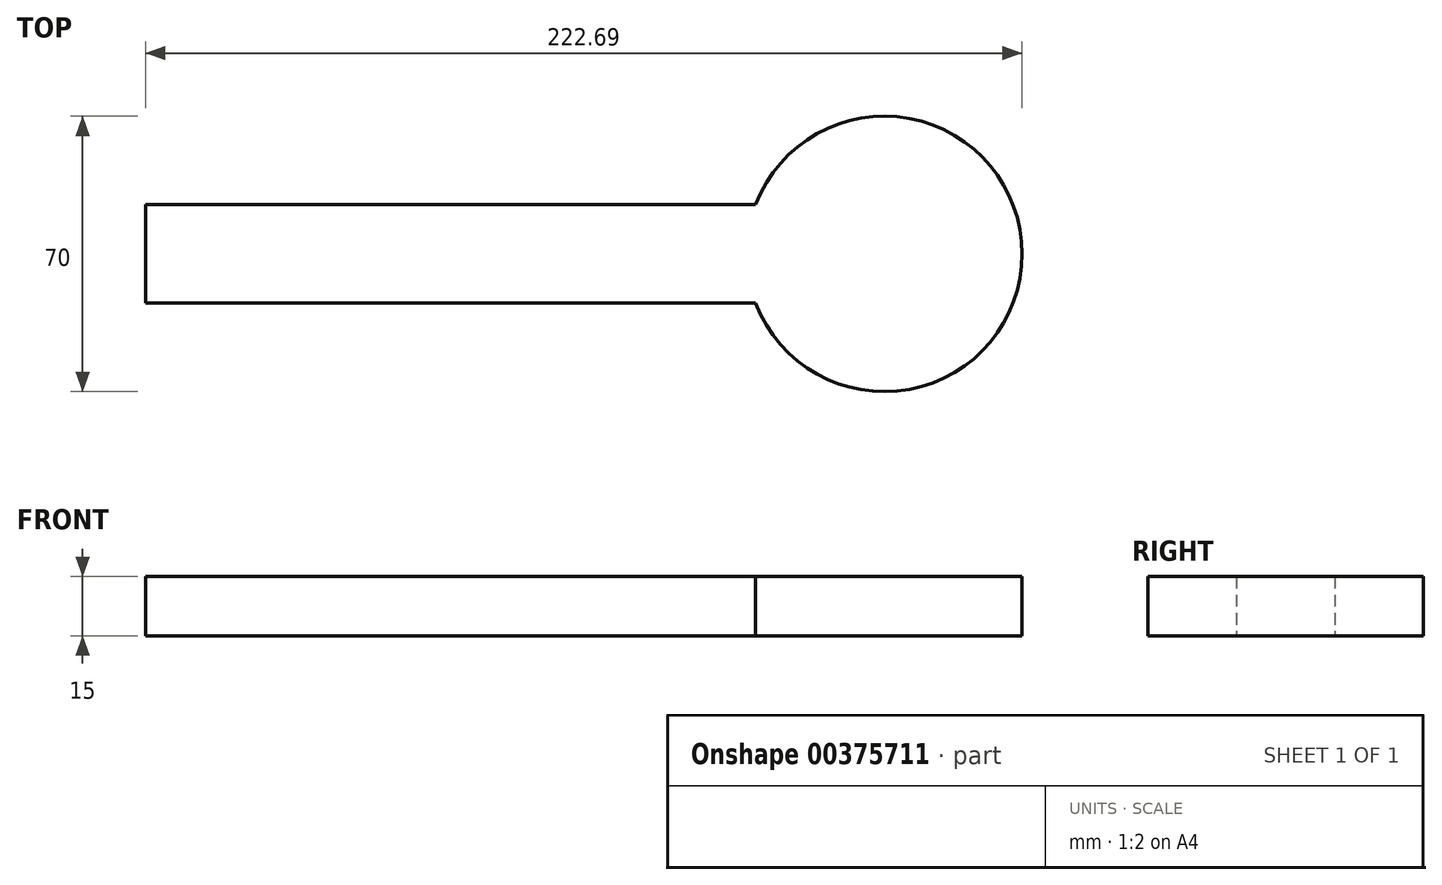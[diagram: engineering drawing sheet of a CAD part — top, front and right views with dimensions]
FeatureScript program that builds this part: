
annotation { "Feature Type Name" : "Feature", "Feature Type Description" : "" }
export const myFeature = defineFeature(function(context is Context, id is Id, definition is map)
    precondition{}
    {
        {
            var Q0;
            Q0=qCreatedBy(makeId("Top.planeOp"),FACE);
            var sketch = newSketch(context, id + "F0", { "sketchPlane" : qUnion([Q0])});
            skLineSegment(sketch, "E0.bottom", {"start": v(-56.63, 41) * mm, "end": v(98.37, 41) * mm});
            skLineSegment(sketch, "E0.top", {"start": v(-56.63, 16) * mm, "end": v(98.37, 16) * mm});
            skLineSegment(sketch, "E0.left", {"start": v(-56.63, 41) * mm, "end": v(-56.63, 16) * mm});
            skLineSegment(sketch, "E0.right", {"start": v(98.37, 41) * mm, "end": v(98.37, 16) * mm});
            skLineSegment(sketch, "E1.bottom", {"start": v(-56.63, 16) * mm, "end": v(-46.63, 16) * mm});
            skLineSegment(sketch, "E1.top", {"start": v(-56.63, -14) * mm, "end": v(-46.63, -14) * mm});
            skLineSegment(sketch, "E1.left", {"start": v(-56.63, 16) * mm, "end": v(-56.63, -14) * mm});
            skLineSegment(sketch, "E1.right", {"start": v(-46.63, 16) * mm, "end": v(-46.63, -14) * mm});
            skLineSegment(sketch, "E2.bottom", {"start": v(-36.63, 16) * mm, "end": v(-28.63, 16) * mm});
            skLineSegment(sketch, "E2.top", {"start": v(-36.63, 1) * mm, "end": v(-28.63, 1) * mm});
            skLineSegment(sketch, "E2.left", {"start": v(-36.63, 16) * mm, "end": v(-36.63, 1) * mm});
            skLineSegment(sketch, "E2.right", {"start": v(-28.63, 16) * mm, "end": v(-28.63, 1) * mm});
            skLineSegment(sketch, "E3", {"start": v(-18.63, 16) * mm, "end": v(-18.63, -15.97) * mm});
            skLineSegment(sketch, "E4", {"start": v(-4.63, 16) * mm, "end": v(-4.63, -15.97) * mm});
            skLineSegment(sketch, "E5", {"start": v(-11.63, 16) * mm, "end": v(-11.63, -14) * mm});
            skLineSegment(sketch, "E6", {"start": v(-18.63, 16) * mm, "end": v(-11.63, 1) * mm});
            skLineSegment(sketch, "E7", {"start": v(-11.63, 1) * mm, "end": v(-4.63, 16) * mm});
            skArc(sketch, "E8", {"start": v(98.37, 16) * mm, "mid": v(166.06, 28.5) * mm, "end": v(98.37, 41) * mm});
            skCircle(sketch, "E9", {"center": v(131.06, 28.5) * mm, "radius": 17.5 * mm});
            skLineSegment(sketch, "E10", {"start": v(131.06, 28.5) * mm, "end": v(-56.63, 28.5) * mm, "construction": true});
            skSolve(sketch);
        }
        {
            var Q0;
            Q0=makeQuery(id+"F0.imprint","IMPRINT",FACE,{"disambiguationData":[TD([[makeQuery(id+"F0.imprint","IMPRINT",EDGE,{"derivedFrom":sQuery(id+"F0.wireOp",EDGE,"E1.bottom")}),-1.0]])]});
            var Q1;
            Q1=makeQuery(id+"F0.imprint","IMPRINT",FACE,{"disambiguationData":[TD([[makeQuery(id+"F0.imprint","IMPRINT",EDGE,{"derivedFrom":sQuery(id+"F0.wireOp",EDGE,"E2.bottom")}),-1.0]])]});
            var Q2;
            Q2=makeQuery(id+"F0.imprint","IMPRINT",FACE,{"disambiguationData":[TD([[makeQuery(id+"F0.imprint","IMPRINT",EDGE,{"derivedFrom":sQuery(id+"F0.wireOp",EDGE,"E0.bottom")}),-1.0]])]});
            var Q3;
            Q3=makeQuery(id+"F0.imprint","IMPRINT",FACE,{"disambiguationData":[TD([[makeQuery(id+"F0.imprint","IMPRINT",EDGE,{"derivedFrom":sQuery(id+"F0.wireOp",EDGE,"E9")}),1.0]])]});
            var Q4;
            Q4=makeQuery(id+"F0.imprint","IMPRINT",FACE,{"disambiguationData":[TD([[makeQuery(id+"F0.imprint","IMPRINT",EDGE,{"derivedFrom":sQuery(id+"F0.wireOp",EDGE,"E0.right")}),1.0]])]});
            extrude(context, id + "F1", {"entities" : qUnion([Q0, Q1, Q2, Q3, Q4]), "depth" : 15 * mm});
        }
    });
